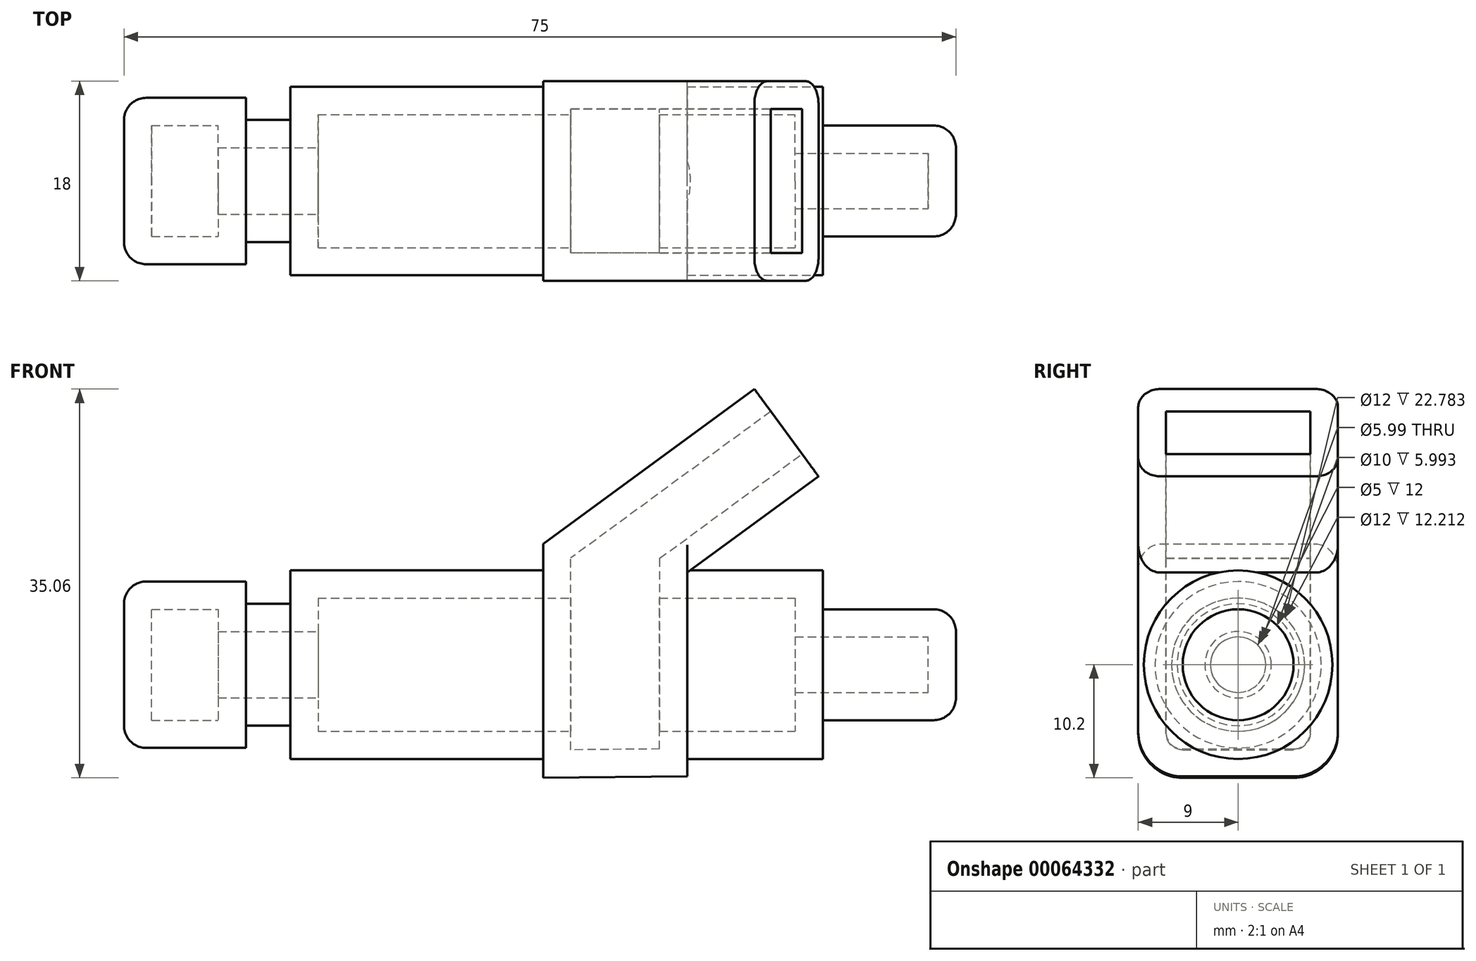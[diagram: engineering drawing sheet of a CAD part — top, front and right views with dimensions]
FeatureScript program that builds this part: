
annotation { "Feature Type Name" : "Feature", "Feature Type Description" : "" }
export const myFeature = defineFeature(function(context is Context, id is Id, definition is map)
    precondition{}
    {
        {
            var Q0;
            Q0=qCreatedBy(makeId("Front.planeOp"),FACE);
            var sketch = newSketch(context, id + "F0", { "sketchPlane" : qUnion([Q0])});
            skLineSegment(sketch, "E0.bottom", {"start": v(0, 0) * mm, "end": v(75, 0) * mm});
            skLineSegment(sketch, "E0.top", {"start": v(0, 8.5) * mm, "end": v(75, 8.5) * mm});
            skLineSegment(sketch, "E0.left", {"start": v(0, 0) * mm, "end": v(0, 8.5) * mm});
            skLineSegment(sketch, "E0.right", {"start": v(75, 0) * mm, "end": v(75, 8.5) * mm});
            skLineSegment(sketch, "E1", {"start": v(0, 0) * mm, "end": v(-54.77, 0) * mm, "construction": true});
            skLineSegment(sketch, "E2.bottom", {"start": v(0, 8.5) * mm, "end": v(15, 8.5) * mm});
            skLineSegment(sketch, "E2.top", {"start": v(0, 7.5) * mm, "end": v(15, 7.5) * mm});
            skLineSegment(sketch, "E2.left", {"start": v(0, 8.5) * mm, "end": v(0, 7.5) * mm});
            skLineSegment(sketch, "E2.right", {"start": v(15, 8.5) * mm, "end": v(15, 7.5) * mm});
            skLineSegment(sketch, "E3.bottom", {"start": v(63, 8.5) * mm, "end": v(75, 8.5) * mm});
            skLineSegment(sketch, "E3.top", {"start": v(63, 5) * mm, "end": v(75, 5) * mm});
            skLineSegment(sketch, "E3.left", {"start": v(63, 8.5) * mm, "end": v(63, 5) * mm});
            skLineSegment(sketch, "E3.right", {"start": v(75, 8.5) * mm, "end": v(75, 5) * mm});
            skLineSegment(sketch, "E4.bottom", {"start": v(15, 7.5) * mm, "end": v(11, 7.5) * mm});
            skLineSegment(sketch, "E4.top", {"start": v(15, 5.5) * mm, "end": v(11, 5.5) * mm});
            skLineSegment(sketch, "E4.left", {"start": v(15, 7.5) * mm, "end": v(15, 5.5) * mm});
            skLineSegment(sketch, "E4.right", {"start": v(11, 7.5) * mm, "end": v(11, 5.5) * mm});
            skSolve(sketch);
        }
        {
            var Q0;
            {var subQ6=sQuery(id+"F0.wireOp",EDGE,"E0.bottom");Q0=makeQuery(id+"F0.imprint","IMPRINT",FACE,{"disambiguationData":[TD([[makeQuery(id+"F0.imprint","IMPRINT",EDGE,{"derivedFrom":subQ6}),1.0]])]});}
            var Q1;
            Q1=sQuery(id+"F0.wireOp",EDGE,"E1");
            revolve(context, id + "F1", {"entities" : qUnion([Q0]), "axis" : qUnion([Q1]), "revolveType" : RevolveType.FULL});
        }
        {
            var Q0;
            Q0=qCreatedBy(makeId("Front.planeOp"),FACE);
            var sketch = newSketch(context, id + "F2", { "sketchPlane" : qUnion([Q0])});
            skLineSegment(sketch, "E5", {"start": v(37.78, -10.2) * mm, "end": v(37.78, 10.89) * mm});
            skLineSegment(sketch, "E6", {"start": v(37.78, 10.89) * mm, "end": v(56.84, 24.86) * mm});
            skLineSegment(sketch, "E7", {"start": v(56.84, 24.86) * mm, "end": v(62.61, 16.98) * mm});
            skLineSegment(sketch, "E8", {"start": v(62.61, 16.98) * mm, "end": v(50.79, 8.31) * mm});
            skLineSegment(sketch, "E9", {"start": v(50.79, 8.31) * mm, "end": v(50.79, -10.07) * mm});
            skLineSegment(sketch, "E10", {"start": v(50.79, -10.07) * mm, "end": v(37.78, -10.2) * mm});
            skSolve(sketch);
        }
        {
            var Q0;
            Q0=qSketchRegion(id+"F2",true);
            extrude(context, id + "F3", {"entities" : qUnion([Q0]), "operationType" : NewBodyOperationType.ADD, "endBound" : BoundingType.SYMMETRIC, "depth" : 18 * mm});
        }
        {
            var Q0;
            Q0=makeQuery(id+"F3.opExtrude","CAP_EDGE",EDGE,{"disambiguationData":[OSD([sQuery(id+"F2.wireOp",EDGE,"E10")])],"isStart":false});
            var Q1;
            Q1=makeQuery(id+"F3.opExtrude","CAP_EDGE",EDGE,{"disambiguationData":[OSD([sQuery(id+"F2.wireOp",EDGE,"E10")])],"isStart":true});
            fillet(context, id + "F4", {"entities" : qUnion([Q0, Q1]), "radius" : 4 * mm, "tangentPropagation" : true, "allowEdgeOverflow" : false});
        }
        {
            var Q0;
            Q0=makeQuery(id+"F1.opRevolve","SWEPT_EDGE",EDGE,{"disambiguationData":[OSD([sQuery(id+"F0.wireOp",EDGE,"E0.left"),sQuery(id+"F0.wireOp",EDGE,"E2.top")])]});
            var Q1;
            Q1=makeQuery(id+"F3.opExtrude","CAP_EDGE",EDGE,{"disambiguationData":[OSD([sQuery(id+"F2.wireOp",EDGE,"E6")])],"isStart":true});
            var Q2;
            Q2=makeQuery(id+"F3.opExtrude","CAP_EDGE",EDGE,{"disambiguationData":[OSD([sQuery(id+"F2.wireOp",EDGE,"E8")])],"isStart":true});
            var Q3;
            Q3=makeQuery(id+"F3.opExtrude","CAP_EDGE",EDGE,{"disambiguationData":[OSD([sQuery(id+"F2.wireOp",EDGE,"E6")])],"isStart":false});
            var Q4;
            Q4=makeQuery(id+"F3.opExtrude","CAP_EDGE",EDGE,{"disambiguationData":[OSD([sQuery(id+"F2.wireOp",EDGE,"E8")])],"isStart":false});
            var Q5;
            Q5=makeQuery(id+"F1.opRevolve","SWEPT_EDGE",EDGE,{"disambiguationData":[OSD([sQuery(id+"F0.wireOp",EDGE,"E0.right"),sQuery(id+"F0.wireOp",EDGE,"E3.top")])]});
            fillet(context, id + "F5", {"entities" : qUnion([Q0, Q1, Q2, Q3, Q4, Q5]), "radius" : 2 * mm, "tangentPropagation" : true, "allowEdgeOverflow" : false});
        }
        {
            var Q0;
            Q0=makeQuery(id+"F3.opExtrude","SWEPT_FACE",FACE,{"disambiguationData":[OSD([sQuery(id+"F2.wireOp",EDGE,"E7")])]});
            shell(context, id + "F6", {"entities" : qUnion([Q0]), "thickness" : 2.5 * mm});
        }
    });
